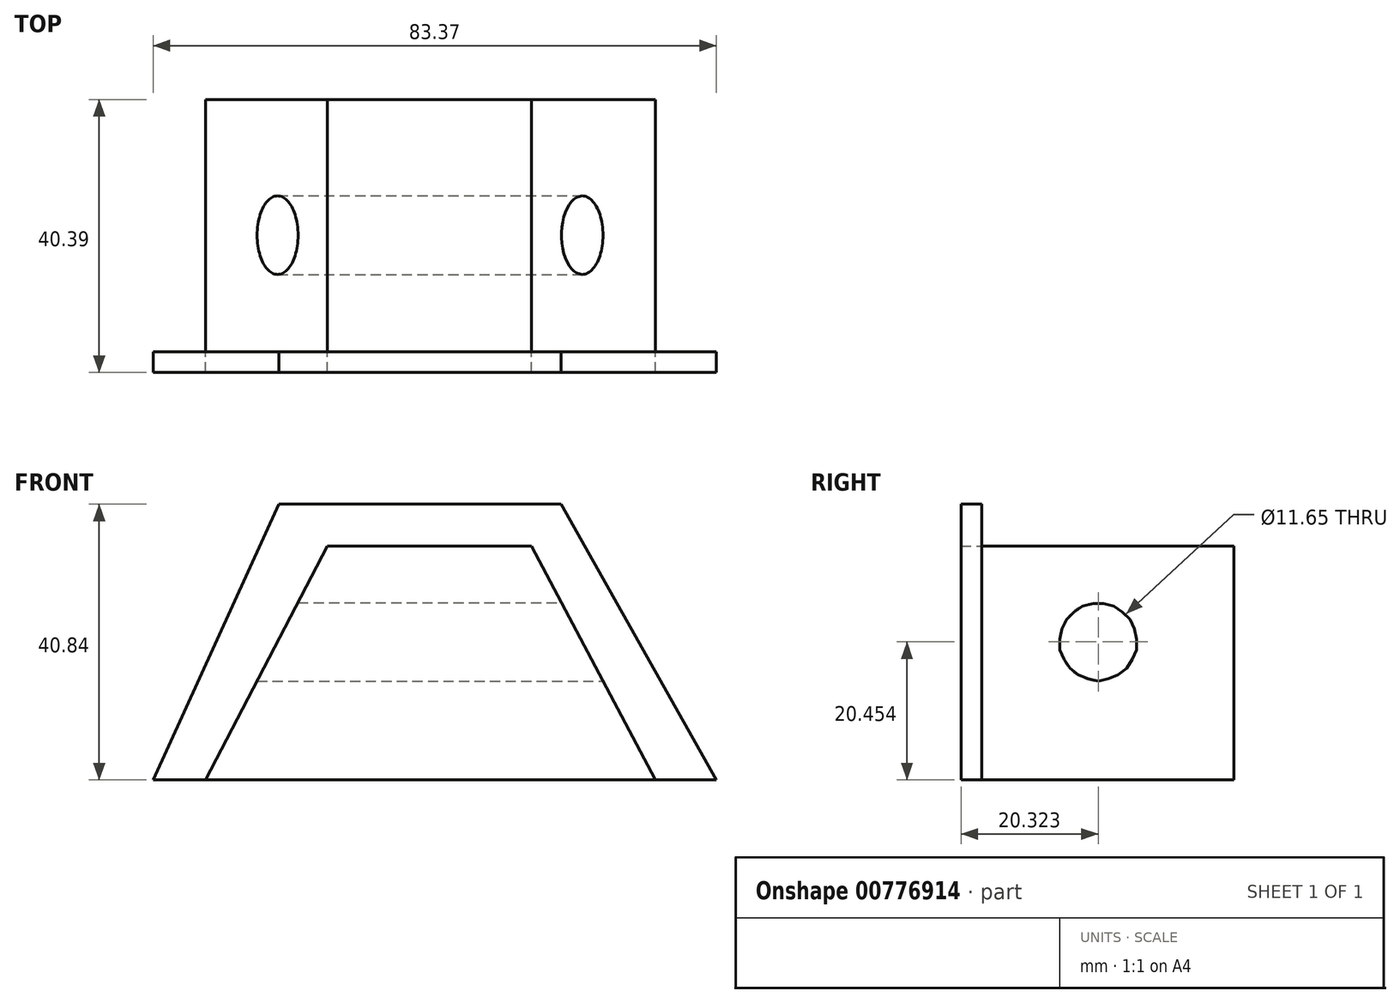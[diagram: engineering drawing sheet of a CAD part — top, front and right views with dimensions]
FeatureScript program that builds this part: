
annotation { "Feature Type Name" : "Feature", "Feature Type Description" : "" }
export const myFeature = defineFeature(function(context is Context, id is Id, definition is map)
    precondition{}
    {
        {
            var Q0;
            Q0=qCreatedBy(makeId("Front.planeOp"),FACE);
            var sketch = newSketch(context, id + "F0", { "sketchPlane" : qUnion([Q0])});
            skLineSegment(sketch, "E0", {"start": v(-30.9, 0) * mm, "end": v(35.68, 0) * mm});
            skLineSegment(sketch, "E1", {"start": v(35.68, 0) * mm, "end": v(17.36, 34.65) * mm});
            skLineSegment(sketch, "E2", {"start": v(17.36, 34.65) * mm, "end": v(-12.84, 34.65) * mm});
            skLineSegment(sketch, "E3", {"start": v(-12.84, 34.65) * mm, "end": v(-30.9, 0) * mm});
            skSolve(sketch);
        }
        {
            var Q0;
            Q0 = qSketchRegion(id + "F0", true);
            extrude(context, id + "F1", {"entities" : qUnion([Q0]), "depth" : 37.34 * mm, "offsetDistance" : 25.4 * mm});
        }
        {
            var Q0;
            Q0=qCreatedBy(makeId("Right.planeOp"),FACE);
            var sketch = newSketch(context, id + "F2", { "sketchPlane" : qUnion([Q0])});
            skCircle(sketch, "E4", {"center": v(-20.07, 20.45) * mm, "radius": 5.82 * mm});
            skSolve(sketch);
        }
        {
            var Q0;
            Q0 = qSketchRegion(id + "F2", true);
            extrude(context, id + "F3", {"entities" : qUnion([Q0]), "operationType" : NewBodyOperationType.REMOVE, "endBound" : BoundingType.SYMMETRIC, "oppositeDirection" : true, "depth" : 59.94 * mm, "offsetDistance" : 25.4 * mm});
        }
        {
            var Q0;
            Q0=makeQuery(id+"F1.opExtrude","CAP_FACE",FACE,{"disambiguationData":[OSD([sQuery(id+"F0.wireOp",EDGE,"E0"),sQuery(id+"F0.wireOp",EDGE,"E1"),sQuery(id+"F0.wireOp",EDGE,"E2"),sQuery(id+"F0.wireOp",EDGE,"E3")])],"isStart":false});
            var sketch = newSketch(context, id + "F4", { "sketchPlane" : qUnion([Q0])});
            skLineSegment(sketch, "E5", {"start": v(-38.65, 0) * mm, "end": v(44.72, 0) * mm});
            skLineSegment(sketch, "E6", {"start": v(44.72, 0) * mm, "end": v(21.74, 40.84) * mm});
            skLineSegment(sketch, "E7", {"start": v(21.74, 40.84) * mm, "end": v(-20.07, 40.84) * mm});
            skLineSegment(sketch, "E8", {"start": v(-20.07, 40.84) * mm, "end": v(-38.65, 0) * mm});
            skSolve(sketch);
        }
        {
            var Q0;
            {var subQ0=sQuery(id+"F4.wireOp",EDGE,"E6");Q0=makeQuery(id+"F4.imprint","IMPRINT",FACE,{"disambiguationData":[TD([[makeQuery(id+"F4.imprint","IMPRINT",EDGE,{"derivedFrom":subQ0}),1.0]])]});}
            extrude(context, id + "F5", {"entities" : qUnion([Q0]), "depth" : 3.05 * mm, "offsetDistance" : 25.4 * mm});
        }
    });
